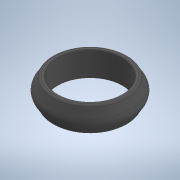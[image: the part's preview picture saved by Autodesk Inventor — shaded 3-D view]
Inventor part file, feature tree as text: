
AUTODESK INVENTOR PART (.ipt)
format: ipt  version: 2020 (Build 240168000, 168)  size: 165,888 bytes
history: native  units: mm
features: revolve x1, chamfer x1, sketch x1
ambient origin geometry x8: Origin, YZ Plane, XZ Plane, XY Plane, X Axis, Y Axis, Z Axis, Center Point
bodies: Solid1 (feature_tree)
feature tree (3):
  revolve  "Revolution1"  [1 undecoded]
  chamfer  "Chamfer1"  Distance=0.8mm
  sketch  "Sketch1"  dims[d0=5.0mm d1=6.45mm d2=0.8mm d3=1.5mm d4=0.5mm d5=2.0mm d6=90.0deg d7=0.1mm d8=2.0mm d9=45.0deg]
note: 1 required parameter value undecoded (feature->parameter linkage not recoverable at this tier; creation-order binding heuristic only, values carry confidence <= 0.55)
